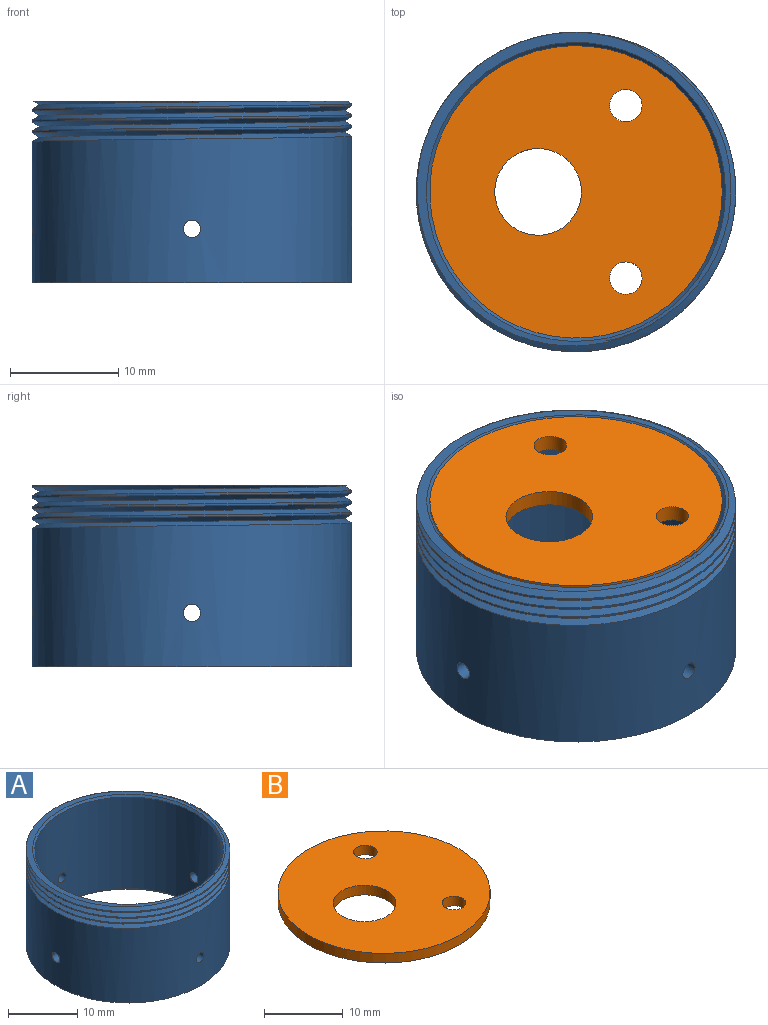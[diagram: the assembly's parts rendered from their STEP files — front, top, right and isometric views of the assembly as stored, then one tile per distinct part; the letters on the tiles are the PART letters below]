
ASSEMBLY  parts=2 mates=1
PART A: 17 faces, bbox 30x34.6x17.9 mm
  f0: cylinder r=14.75mm len=29.5mm, axis (0,0,-1), area 1201.4mm2, adj f1,f7,f8,f9,f13,f14,f15,f16
  f1: cylinder r=14.75mm len=29.5mm, axis (0,0,-1), area 18.5mm2, adj f0,f2,f9,f10
  f2: cylinder r=14.75mm len=29.5mm, axis (0,0,-1), area 18.5mm2, adj f1,f3,f9,f10
  f3: cylinder r=14.75mm len=29.5mm, axis (0,0,-1), area 18.5mm2, adj f2,f4,f9,f10
  f4: cylinder r=14.75mm len=28.74mm, axis (0,0,-1), area 6.5mm2, adj f3,f6,f9,f10
  f5: cylinder r=13.5mm len=27mm, axis (0,0,-1), area 1366.1mm2, adj f11,f12,f13,f14,f15,f16
  f6: plane 29.52x29.52mm, normal (0,0,1), area 59.9mm2, adj f4,f9,f10,f11
  f7: plane 29.5x29.5mm, normal (0,0,-1), area 85.2mm2, adj f0,f12
  f8: plane 0.8x0.69mm, normal (0,1,0), area 0.3mm2, adj f0,f9,f10
  f9: bspline ~34.06x29.5mm, area 293.4mm2, adj f0,f1,f2,f3,f4,f6,f8,f10
  f10: bspline ~34.06x29.5mm, area 264mm2, adj f1,f2,f3,f4,f6,f8,f9
  f11: cone r=13.5mm half-angle=45deg, axis (0,0,1), area 36.4mm2, adj f5,f6
  f12: cone r=13.8mm half-angle=45deg, axis (0,0,-1), area 36.4mm2, adj f5,f7
  f13: cylinder r=0.8mm len=1.6mm, axis (0,-1,0), area 6.3mm2, adj f0,f5
  f14: cylinder r=0.8mm len=1.6mm, axis (0,-1,0), area 6.3mm2, adj f0,f5
  f15: cylinder r=0.8mm len=1.6mm, axis (1,0,0), area 6.3mm2, adj f0,f5
  f16: cylinder r=0.8mm len=1.6mm, axis (1,0,0), area 6.3mm2, adj f0,f5
PART B: 6 faces, bbox 27x27x1.5 mm
  f0: cylinder r=13.5mm len=27mm, axis (0,0,-1), area 127.2mm2, adj f2,f3
  f1: cylinder r=4mm len=8mm, axis (0,0,-1), area 37.7mm2, adj f2,f3
  f2: plane 27x27mm, normal (0,0,1), area 508.2mm2, adj f0,f1,f4,f5
  f3: plane 27x27mm, normal (0,0,-1), area 508.2mm2, adj f0,f1,f4,f5
  f4: cylinder r=1.5mm len=3mm, axis (0,0,-1), area 14.1mm2, adj f2,f3
  f5: cylinder r=1.5mm len=3mm, axis (0,0,-1), area 14.1mm2, adj f2,f3
PLACE A t=(2.44,-1.01,-4.44)mm
PLACE B t=(2.44,-1.31,10.86)mm
MATE fastened B.f0 <-> A.f0  axis (0,0,1) through (2.44,-1.01,12.36)mm
